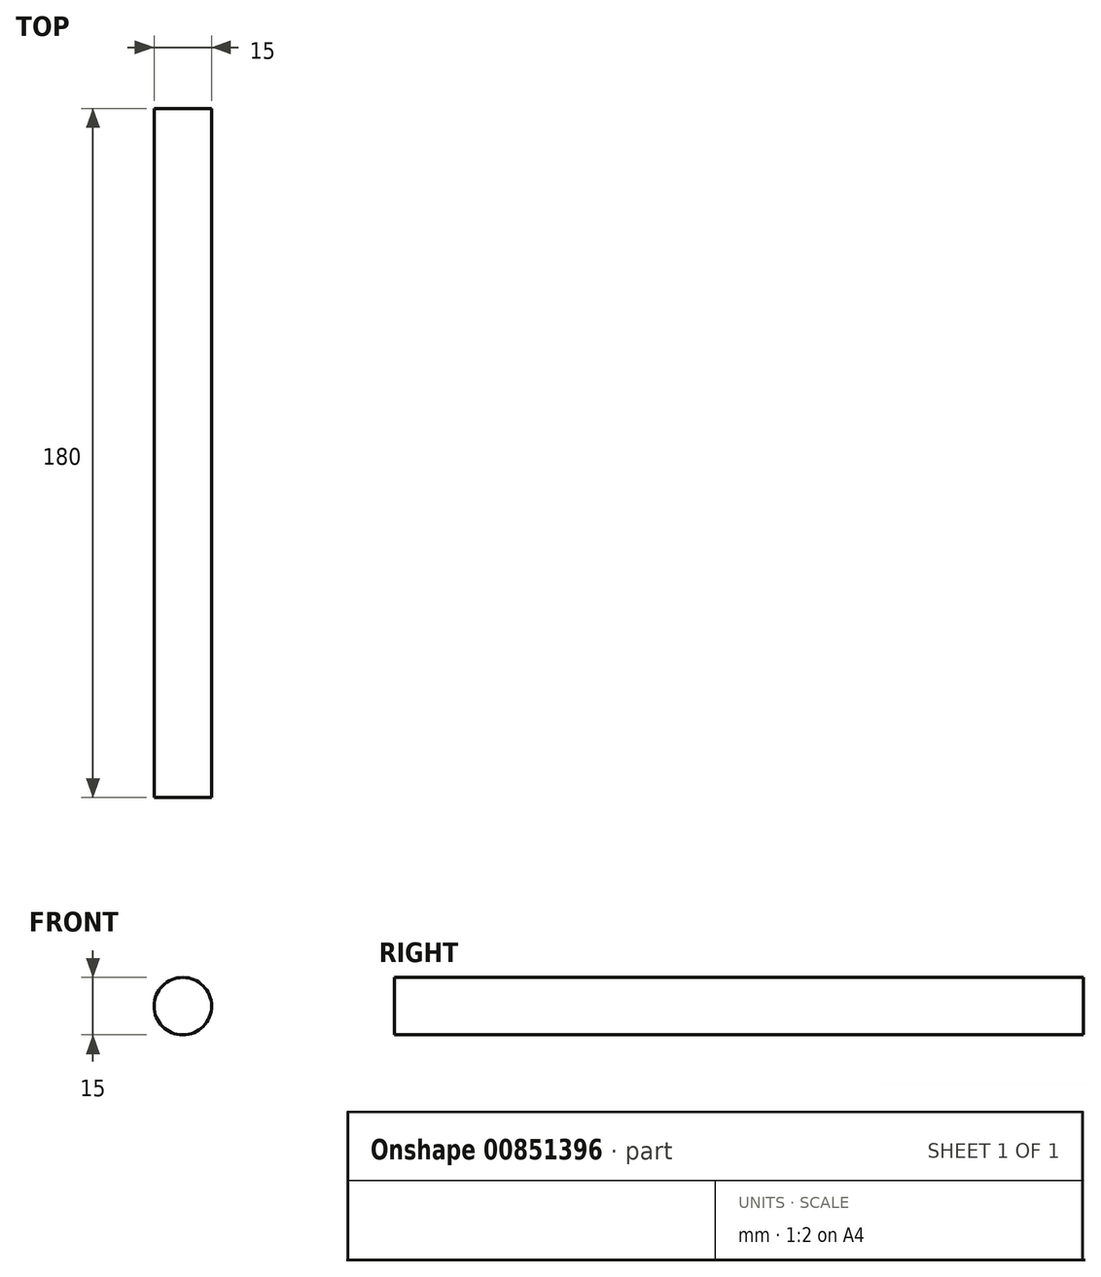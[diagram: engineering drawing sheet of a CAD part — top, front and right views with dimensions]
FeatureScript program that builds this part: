
annotation { "Feature Type Name" : "Feature", "Feature Type Description" : "" }
export const myFeature = defineFeature(function(context is Context, id is Id, definition is map)
    precondition{}
    {
        {
            var Q0;
            Q0=qCreatedBy(makeId("Front.planeOp"),FACE);
            var sketch = newSketch(context, id + "F0", { "sketchPlane" : qUnion([Q0])});
            skCircle(sketch, "E0", {"center": v(0, 0) * mm, "radius": 7.5 * mm});
            skSolve(sketch);
        }
        {
            var Q0;
            Q0=makeQuery(id+"F0.imprint","IMPRINT",FACE,{"disambiguationData":[TD([[makeQuery(id+"F0.imprint","IMPRINT",EDGE,{"derivedFrom":sQuery(id+"F0.wireOp",EDGE,"E0")}),1.0]])]});
            extrude(context, id + "F1", {"entities" : qUnion([Q0]), "endBound" : BoundingType.SYMMETRIC, "depth" : 180 * mm, "offsetDistance" : 25 * mm});
        }
    });
